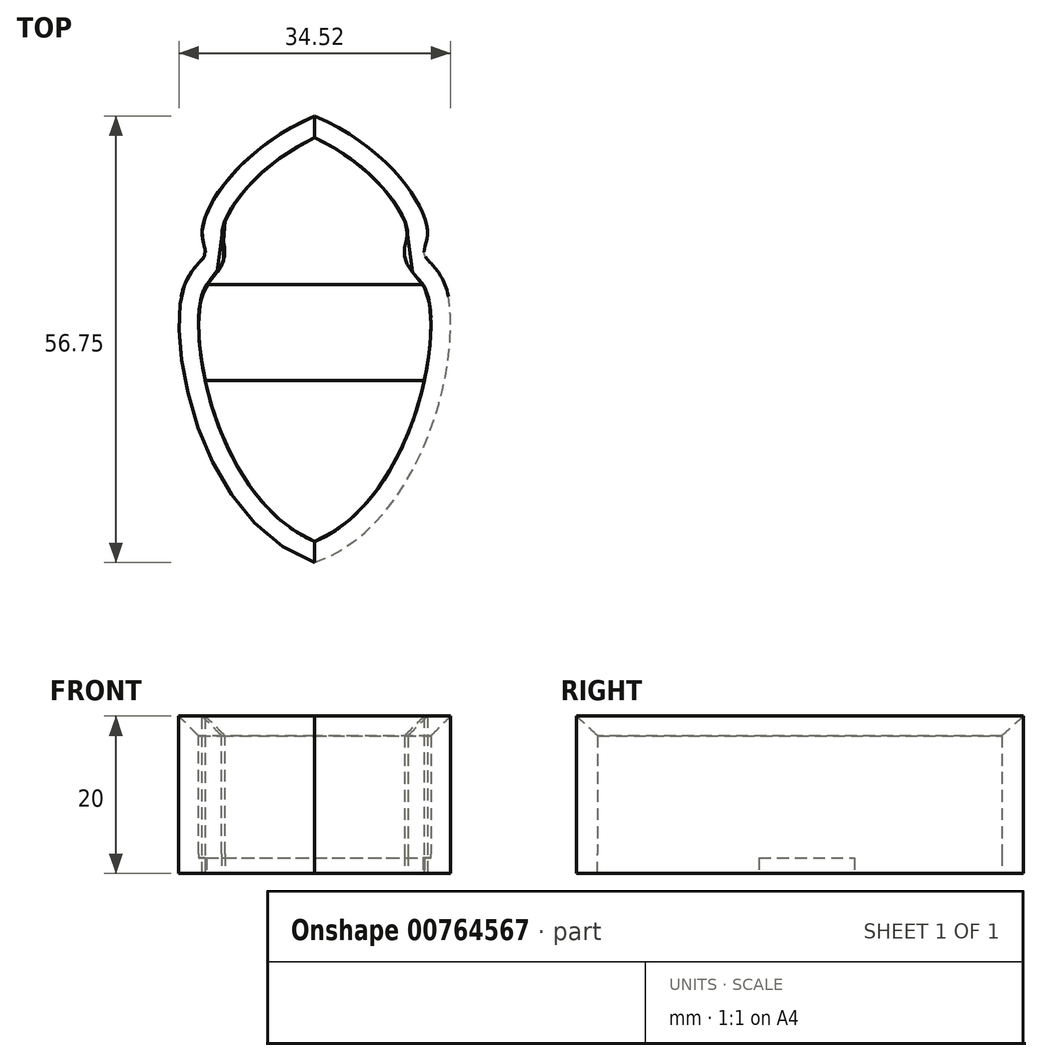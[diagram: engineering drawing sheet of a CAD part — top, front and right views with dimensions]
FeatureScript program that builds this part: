
annotation { "Feature Type Name" : "Feature", "Feature Type Description" : "" }
export const myFeature = defineFeature(function(context is Context, id is Id, definition is map)
    precondition{}
    {
        {
            var Q0;
            Q0=qCreatedBy(makeId("Top.planeOp"),FACE);
            var sketch = newSketch(context, id + "F0", { "sketchPlane" : qUnion([Q0])});
            skFitSpline(sketch, "E0", {"points": [v(0, 0) * mm, v(-16.75, 34.68) * mm, v(-13.93, 39.17) * mm, v(-14.32, 42) * mm, v(0, 56.75) * mm], "startDerivative": vector(-101.52, 36.2) * mm, "endDerivative": vector(90.75, 39.47) * mm});
            skFitSpline(sketch, "E1.MirrorCS", {"points": [v(0, 0) * mm, v(16.75, 34.68) * mm, v(13.93, 39.17) * mm, v(14.32, 42) * mm, v(0, 56.75) * mm], "startDerivative": vector(101.52, 36.2) * mm, "endDerivative": vector(-90.75, 39.47) * mm});
            skSolve(sketch);
        }
        {
            var Q0;
            Q0=makeQuery(id+"F0.imprint","IMPRINT",FACE,{"disambiguationData":[TD([[makeQuery(id+"F0.imprint","IMPRINT",EDGE,{"derivedFrom":sQuery(id+"F0.wireOp",EDGE,"E0")}),-1.0]])]});
            extrude(context, id + "F1", {"entities" : qUnion([Q0]), "depth" : 20 * mm, "offsetDistance" : 25 * mm});
        }
        {
            var Q0;
            Q0=makeQuery(id+"F1.opExtrude","CAP_FACE",FACE,{"disambiguationData":[OSD([sQuery(id+"F0.wireOp",EDGE,"E0"),sQuery(id+"F0.wireOp",EDGE,"E1.MirrorCS")])],"isStart":false});
            shell(context, id + "F2", {"entities" : qUnion([Q0]), "thickness" : 2.5 * mm});
        }
        {
            var Q0;
            {var subQ0=sQuery(id+"F0.wireOp",EDGE,"E0");Q0=makeQuery(id+"F2.opShell","OFFSET_EDGE",EDGE,{"disambiguationData":[OSD([subQ0]),TDD([makeQuery(id+"F1.opExtrude","CAP_EDGE",EDGE,{"disambiguationData":[OSD([subQ0])],"isStart":false})])]});}
            var Q1;
            {var subQ0=sQuery(id+"F0.wireOp",EDGE,"E1.MirrorCS");Q1=makeQuery(id+"F2.opShell","OFFSET_EDGE",EDGE,{"disambiguationData":[OSD([subQ0]),TDD([makeQuery(id+"F1.opExtrude","CAP_EDGE",EDGE,{"disambiguationData":[OSD([subQ0])],"isStart":false})])]});}
            chamfer(context, id + "F3", {"entities" : qUnion([Q0, Q1]), "width" : 2.5 * mm, "tangentPropagation" : true});
        }
        {
            var Q0;
            Q0=makeQuery(id+"F2.opShell","OFFSET_FACE",FACE,{"disambiguationData":[OSD([sQuery(id+"F0.wireOp",EDGE,"E0"),sQuery(id+"F0.wireOp",EDGE,"E1.MirrorCS")])]});
            extrude(context, id + "F4", {"entities" : qUnion([Q0]), "operationType" : NewBodyOperationType.REMOVE, "endBound" : BoundingType.SYMMETRIC, "depth" : 100 * mm, "offsetDistance" : 25 * mm});
        }
        {
            var Q0;
            Q0=makeQuery(id+"F0.imprint","IMPRINT",FACE,{"disambiguationData":[TD([[makeQuery(id+"F0.imprint","IMPRINT",EDGE,{"derivedFrom":sQuery(id+"F0.wireOp",EDGE,"E0")}),-1.0]])]});
            var sketch = newSketch(context, id + "F5", { "sketchPlane" : qUnion([Q0])});
            skLineSegment(sketch, "E2.bottom", {"start": v(-15.23, 23.16) * mm, "end": v(15.42, 23.16) * mm});
            skLineSegment(sketch, "E2.top", {"start": v(-15.23, 35.33) * mm, "end": v(15.42, 35.33) * mm});
            skLineSegment(sketch, "E2.left", {"start": v(-15.23, 23.16) * mm, "end": v(-15.23, 35.33) * mm});
            skLineSegment(sketch, "E2.right", {"start": v(15.42, 23.16) * mm, "end": v(15.42, 35.33) * mm});
            skSolve(sketch);
        }
        {
            var Q0;
            Q0=makeQuery(id+"F5.imprint","IMPRINT",FACE,{"disambiguationData":[TD([[makeQuery(id+"F5.imprint","IMPRINT",EDGE,{"derivedFrom":sQuery(id+"F5.wireOp",EDGE,"E2.bottom")}),1.0]])]});
            extrude(context, id + "F6", {"entities" : qUnion([Q0]), "operationType" : NewBodyOperationType.ADD, "depth" : 2 * mm, "offsetDistance" : 25 * mm});
        }
    });
